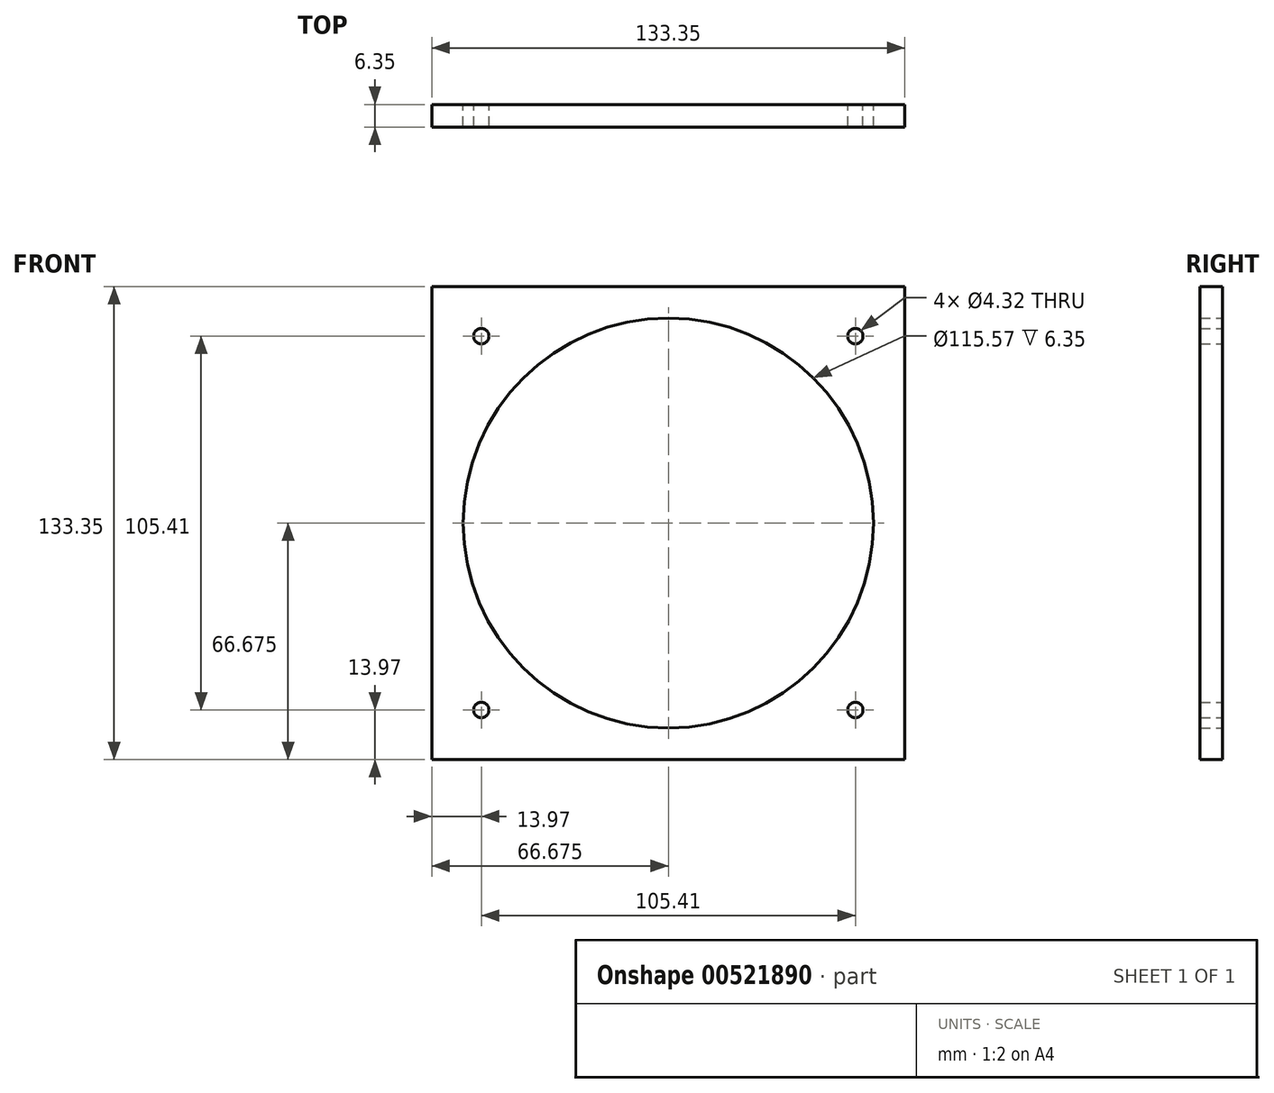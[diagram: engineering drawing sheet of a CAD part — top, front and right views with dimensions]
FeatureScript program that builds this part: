
annotation { "Feature Type Name" : "Feature", "Feature Type Description" : "" }
export const myFeature = defineFeature(function(context is Context, id is Id, definition is map)
    precondition{}
    {
        {
            var Q0;
            Q0=qCreatedBy(makeId("Front.planeOp"),FACE);
            var sketch = newSketch(context, id + "F0", { "sketchPlane" : qUnion([Q0])});
            skLineSegment(sketch, "E0.bottom", {"start": v(0, 0) * mm, "end": v(133.35, 0) * mm});
            skLineSegment(sketch, "E0.top", {"start": v(0, 133.35) * mm, "end": v(133.35, 133.35) * mm});
            skLineSegment(sketch, "E0.left", {"start": v(0, 0) * mm, "end": v(0, 133.35) * mm});
            skLineSegment(sketch, "E0.right", {"start": v(133.35, 0) * mm, "end": v(133.35, 133.35) * mm});
            skLineSegment(sketch, "E1.0", {"start": v(6.35, 6.35) * mm, "end": v(6.35, 127) * mm, "construction": true});
            skLineSegment(sketch, "E2.0", {"start": v(127, 6.35) * mm, "end": v(127, 127) * mm, "construction": true});
            skLineSegment(sketch, "E3.0", {"start": v(6.35, 127) * mm, "end": v(127, 127) * mm, "construction": true});
            skLineSegment(sketch, "E4.0", {"start": v(6.35, 6.35) * mm, "end": v(127, 6.35) * mm, "construction": true});
            skLineSegment(sketch, "E5", {"start": v(6.35, 127) * mm, "end": v(127, 6.35) * mm, "construction": true});
            skLineSegment(sketch, "E6", {"start": v(127, 127) * mm, "end": v(6.35, 6.35) * mm, "construction": true});
            skCircle(sketch, "E7", {"center": v(66.68, 66.68) * mm, "radius": 57.79 * mm});
            skCircle(sketch, "E8", {"center": v(119.38, 119.38) * mm, "radius": 2.16 * mm});
            skCircle(sketch, "E9", {"center": v(13.97, 119.38) * mm, "radius": 2.16 * mm});
            skCircle(sketch, "E10", {"center": v(13.97, 13.97) * mm, "radius": 2.16 * mm});
            skCircle(sketch, "E11", {"center": v(119.38, 13.97) * mm, "radius": 2.16 * mm});
            skSolve(sketch);
        }
        {
            var Q0;
            Q0=makeQuery(id+"F0.imprint","IMPRINT",FACE,{"disambiguationData":[TD([[makeQuery(id+"F0.imprint","IMPRINT",EDGE,{"derivedFrom":sQuery(id+"F0.wireOp",EDGE,"E0.bottom")}),1.0]])]});
            extrude(context, id + "F1", {"entities" : qUnion([Q0]), "depth" : 6.35 * mm, "offsetDistance" : 25.4 * mm});
        }
    });
